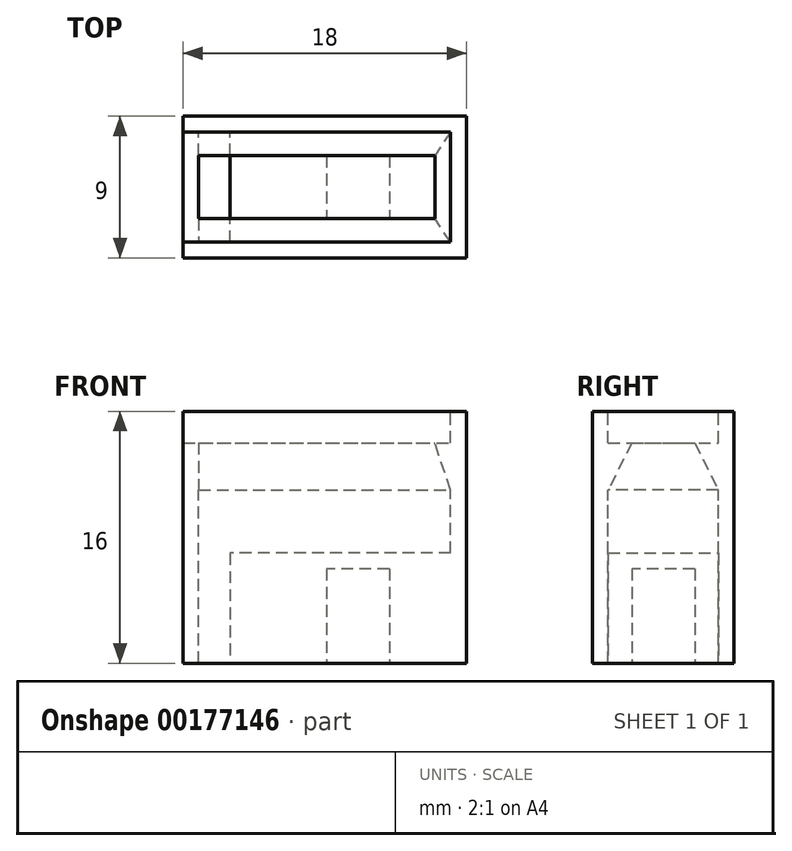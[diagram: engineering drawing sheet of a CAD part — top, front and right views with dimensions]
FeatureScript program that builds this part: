
annotation { "Feature Type Name" : "Feature", "Feature Type Description" : "" }
export const myFeature = defineFeature(function(context is Context, id is Id, definition is map)
    precondition{}
    {
        {
            var Q0;
            Q0=qCreatedBy(makeId("Top.planeOp"),FACE);
            var sketch = newSketch(context, id + "F0", { "sketchPlane" : qUnion([Q0])});
            skLineSegment(sketch, "E0.bottom", {"start": v(9, -4.5) * mm, "end": v(-9, -4.5) * mm});
            skLineSegment(sketch, "E0.top", {"start": v(9, 4.5) * mm, "end": v(-9, 4.5) * mm});
            skLineSegment(sketch, "E0.left", {"start": v(9, -4.5) * mm, "end": v(9, 4.5) * mm});
            skLineSegment(sketch, "E0.right", {"start": v(-9, -4.5) * mm, "end": v(-9, 4.5) * mm});
            skPoint(sketch, "E0.middle", {"position": v(0, 0) * mm});
            skSolve(sketch);
        }
        {
            var Q0;
            Q0=qSketchRegion(id+"F0",true);
            extrude(context, id + "F1", {"entities" : qUnion([Q0]), "depth" : 14 * mm});
        }
        {
            var Q0;
            Q0=makeQuery(id+"F1.opExtrude","CAP_FACE",FACE,{"disambiguationData":[OSD([sQuery(id+"F0.wireOp",EDGE,"E0.bottom"),sQuery(id+"F0.wireOp",EDGE,"E0.top"),sQuery(id+"F0.wireOp",EDGE,"E0.left"),sQuery(id+"F0.wireOp",EDGE,"E0.right")])],"isStart":false});
            var sketch = newSketch(context, id + "F2", { "sketchPlane" : qUnion([Q0])});
            skLineSegment(sketch, "E1.bottom", {"start": v(8, -3.5) * mm, "end": v(-8, -3.5) * mm});
            skLineSegment(sketch, "E1.top", {"start": v(8, 3.5) * mm, "end": v(-8, 3.5) * mm});
            skLineSegment(sketch, "E1.left", {"start": v(8, -3.5) * mm, "end": v(8, 3.5) * mm});
            skLineSegment(sketch, "E1.right", {"start": v(-8, -3.5) * mm, "end": v(-8, 3.5) * mm});
            skPoint(sketch, "E1.middle", {"position": v(0, 0) * mm});
            skSolve(sketch);
        }
        {
            var Q0;
            Q0=qSketchRegion(id+"F2",true);
            extrude(context, id + "F3", {"entities" : qUnion([Q0]), "operationType" : NewBodyOperationType.REMOVE, "oppositeDirection" : true, "depth" : 7 * mm});
        }
        {
            var Q0;
            Q0=makeQuery(id+"F1.opExtrude","CAP_FACE",FACE,{"disambiguationData":[OSD([sQuery(id+"F0.wireOp",EDGE,"E0.bottom"),sQuery(id+"F0.wireOp",EDGE,"E0.top"),sQuery(id+"F0.wireOp",EDGE,"E0.left"),sQuery(id+"F0.wireOp",EDGE,"E0.right")])],"isStart":true});
            var sketch = newSketch(context, id + "F4", { "sketchPlane" : qUnion([Q0])});
            skLineSegment(sketch, "E2.bottom", {"start": v(4.1, -2) * mm, "end": v(0.1, -2) * mm});
            skLineSegment(sketch, "E2.top", {"start": v(4.1, 2) * mm, "end": v(0.1, 2) * mm});
            skLineSegment(sketch, "E2.left", {"start": v(4.1, -2) * mm, "end": v(4.1, 2) * mm});
            skLineSegment(sketch, "E2.right", {"start": v(0.1, -2) * mm, "end": v(0.1, 2) * mm});
            skPoint(sketch, "E2.middle", {"position": v(2.1, 0) * mm});
            skLineSegment(sketch, "E3.bottom", {"start": v(-6, -3.5) * mm, "end": v(-8, -3.5) * mm});
            skLineSegment(sketch, "E3.top", {"start": v(-6, 3.5) * mm, "end": v(-8, 3.5) * mm});
            skLineSegment(sketch, "E3.left", {"start": v(-6, -3.5) * mm, "end": v(-6, 3.5) * mm});
            skLineSegment(sketch, "E3.right", {"start": v(-8, -3.5) * mm, "end": v(-8, 3.5) * mm});
            skPoint(sketch, "E3.middle", {"position": v(-7, 0) * mm});
            skSolve(sketch);
        }
        {
            var Q0;
            Q0=makeQuery(id+"F4.imprint","IMPRINT",FACE,{"disambiguationData":[TD([[makeQuery(id+"F4.imprint","IMPRINT",EDGE,{"derivedFrom":sQuery(id+"F4.wireOp",EDGE,"E2.bottom")}),-1.0]])]});
            extrude(context, id + "F5", {"entities" : qUnion([Q0]), "operationType" : NewBodyOperationType.REMOVE, "oppositeDirection" : true, "depth" : 6 * mm});
        }
        {
            var Q0;
            Q0=makeQuery(id+"F4.imprint","IMPRINT",FACE,{"disambiguationData":[TD([[makeQuery(id+"F4.imprint","IMPRINT",EDGE,{"derivedFrom":sQuery(id+"F4.wireOp",EDGE,"E3.bottom")}),-1.0]])]});
            extrude(context, id + "F6", {"entities" : qUnion([Q0]), "operationType" : NewBodyOperationType.REMOVE, "oppositeDirection" : true, "depth" : 9 * mm});
        }
        {
            var Q0;
            Q0=makeQuery(id+"F1.opExtrude","CAP_FACE",FACE,{"disambiguationData":[OSD([sQuery(id+"F0.wireOp",EDGE,"E0.bottom"),sQuery(id+"F0.wireOp",EDGE,"E0.top"),sQuery(id+"F0.wireOp",EDGE,"E0.left"),sQuery(id+"F0.wireOp",EDGE,"E0.right")])],"isStart":false});
            var sketch = newSketch(context, id + "F7", { "sketchPlane" : qUnion([Q0])});
            skLineSegment(sketch, "E4", {"start": v(-9, 4.5) * mm, "end": v(9, 4.5) * mm});
            skLineSegment(sketch, "E5", {"start": v(9, 4.5) * mm, "end": v(9, -4.5) * mm});
            skLineSegment(sketch, "E6", {"start": v(9, -4.5) * mm, "end": v(-9, -4.5) * mm});
            skLineSegment(sketch, "E7", {"start": v(-9, -4.5) * mm, "end": v(-9, -3.5) * mm});
            skLineSegment(sketch, "E8", {"start": v(-9, -3.5) * mm, "end": v(8, -3.5) * mm});
            skLineSegment(sketch, "E9", {"start": v(8, -3.5) * mm, "end": v(8, 3.5) * mm});
            skLineSegment(sketch, "E10", {"start": v(8, 3.5) * mm, "end": v(-9, 3.5) * mm});
            skLineSegment(sketch, "E11", {"start": v(-9, 3.5) * mm, "end": v(-9, 4.5) * mm});
            skSolve(sketch);
        }
        {
            var Q0;
            Q0=qSketchRegion(id+"F7",true);
            extrude(context, id + "F8", {"entities" : qUnion([Q0]), "operationType" : NewBodyOperationType.ADD, "depth" : 2 * mm});
        }
        {
            var Q0;
            Q0=makeQuery(id+"F8.boolean.opBoolean","MERGE",FACE,{"derivedFrom":[makeQuery(id+"F6.boolean.opBoolean","MERGE",FACE,{"derivedFrom":[makeQuery(id+"F3.boolean.opBoolean","COPY",FACE,{"derivedFrom":makeQuery(id+"F3.opExtrude","SWEPT_FACE",FACE,{"disambiguationData":[OSD([sQuery(id+"F2.wireOp",EDGE,"E1.bottom")])]})}),makeQuery(id+"F6.opExtrude","SWEPT_FACE",FACE,{"disambiguationData":[OSD([sQuery(id+"F4.wireOp",EDGE,"E3.top")])]})]}),makeQuery(id+"F8.opExtrude","SWEPT_FACE",FACE,{"disambiguationData":[OSD([sQuery(id+"F7.wireOp",EDGE,"E8")])]})]});
            var sketch = newSketch(context, id + "F9", { "sketchPlane" : qUnion([Q0])});
            skLineSegment(sketch, "E12", {"start": v(-8, 14) * mm, "end": v(-7, 14) * mm});
            skLineSegment(sketch, "E13", {"start": v(8, 14) * mm, "end": v(6.5, 14) * mm, "construction": true});
            skLineSegment(sketch, "E14", {"start": v(6.5, 14) * mm, "end": v(8, 7) * mm, "construction": true});
            skLineSegment(sketch, "E15", {"start": v(8, 7) * mm, "end": v(8, 14) * mm, "construction": true});
            skLineSegment(sketch, "E16", {"start": v(-7, 14) * mm, "end": v(-8, 11) * mm});
            skLineSegment(sketch, "E17", {"start": v(-8, 11) * mm, "end": v(-8, 14) * mm});
            skSolve(sketch);
        }
        {
            var Q0;
            Q0 = qSketchRegion(id + "F9", true);
            extrude(context, id + "F10", {"entities" : qUnion([Q0]), "depth" : 7 * mm});
        }
        {
            var Q0;
            Q0=makeQuery(id+"F8.boolean.opBoolean","MERGE",FACE,{"derivedFrom":[makeQuery(id+"F3.boolean.opBoolean","COPY",FACE,{"derivedFrom":makeQuery(id+"F3.opExtrude","SWEPT_FACE",FACE,{"disambiguationData":[OSD([sQuery(id+"F2.wireOp",EDGE,"E1.left")])]})}),makeQuery(id+"F8.opExtrude","SWEPT_FACE",FACE,{"disambiguationData":[OSD([sQuery(id+"F7.wireOp",EDGE,"E9")])]})]});
            var sketch = newSketch(context, id + "F11", { "sketchPlane" : qUnion([Q0])});
            skLineSegment(sketch, "E18", {"start": v(3.5, 14) * mm, "end": v(2, 14) * mm});
            skLineSegment(sketch, "E19", {"start": v(-2, 14) * mm, "end": v(-3.5, 14) * mm});
            skLineSegment(sketch, "E20", {"start": v(2, 14) * mm, "end": v(3.5, 11) * mm});
            skLineSegment(sketch, "E21", {"start": v(3.5, 11) * mm, "end": v(3.5, 14) * mm});
            skLineSegment(sketch, "E22", {"start": v(-2, 14) * mm, "end": v(-3.5, 11) * mm});
            skLineSegment(sketch, "E23", {"start": v(-3.5, 11) * mm, "end": v(-3.5, 14) * mm});
            skSolve(sketch);
        }
        {
            var Q0;
            Q0 = qSketchRegion(id + "F11", true);
            extrude(context, id + "F12", {"entities" : qUnion([Q0]), "operationType" : NewBodyOperationType.ADD, "depth" : 16 * mm});
        }
    });
